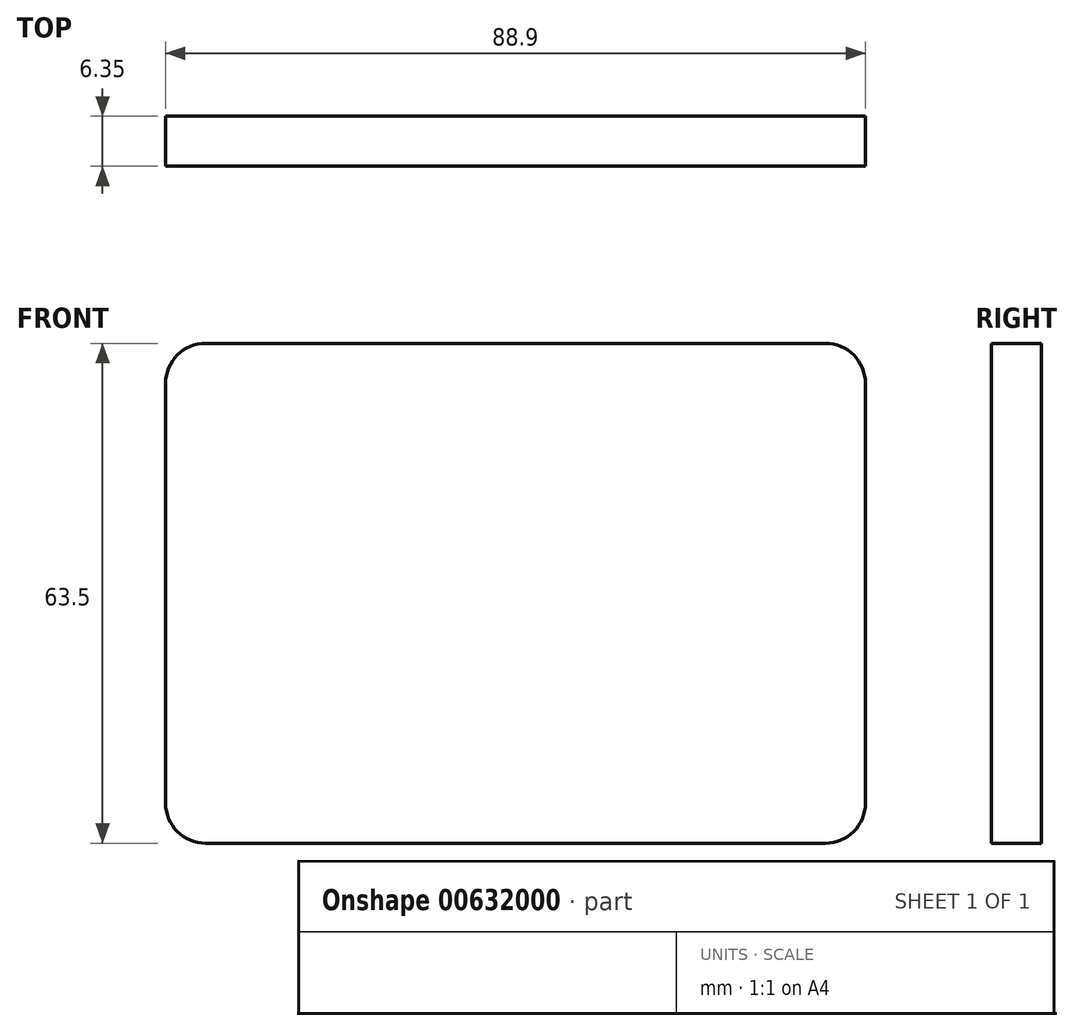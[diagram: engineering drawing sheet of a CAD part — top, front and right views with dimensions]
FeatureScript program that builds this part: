
annotation { "Feature Type Name" : "Feature", "Feature Type Description" : "" }
export const myFeature = defineFeature(function(context is Context, id is Id, definition is map)
    precondition{}
    {
        {
            var Q0;
            Q0=qCreatedBy(makeId("Front.planeOp"),FACE);
            var sketch = newSketch(context, id + "F0", { "sketchPlane" : qUnion([Q0])});
            skLineSegment(sketch, "E0.bottom", {"start": v(0, 0) * mm, "end": v(114.3, 0) * mm});
            skLineSegment(sketch, "E0.top", {"start": v(0, 88.9) * mm, "end": v(114.3, 88.9) * mm});
            skLineSegment(sketch, "E0.left", {"start": v(0, 0) * mm, "end": v(0, 88.9) * mm});
            skLineSegment(sketch, "E0.right", {"start": v(114.3, 0) * mm, "end": v(114.3, 88.9) * mm});
            skLineSegment(sketch, "E1.bottom", {"start": v(0, 0) * mm, "end": v(88.9, 0) * mm});
            skLineSegment(sketch, "E1.top", {"start": v(0, 63.5) * mm, "end": v(88.9, 63.5) * mm});
            skLineSegment(sketch, "E1.left", {"start": v(0, 0) * mm, "end": v(0, 63.5) * mm});
            skLineSegment(sketch, "E1.right", {"start": v(88.9, 0) * mm, "end": v(88.9, 63.5) * mm});
            skCircle(sketch, "E2", {"center": v(101.6, 76.2) * mm, "radius": 3.18 * mm});
            skSolve(sketch);
        }
        {
            var Q0;
            Q0=makeQuery(id+"F0.imprint","IMPRINT",FACE,{"disambiguationData":[TD([[makeQuery(id+"F0.imprint","IMPRINT",EDGE,{"derivedFrom":sQuery(id+"F0.wireOp",EDGE,"E0.bottom")}),1.0]])]});
            extrude(context, id + "F1", {"entities" : qUnion([Q0]), "depth" : 6.35 * mm, "offsetDistance" : 25.4 * mm});
        }
        {
            var Q0;
            Q0=makeQuery(id+"F1.opExtrude","SWEPT_EDGE",EDGE,{"disambiguationData":[OSD([sQuery(id+"F0.wireOp",EDGE,"E0.left"),sQuery(id+"F0.wireOp",EDGE,"E1.top"),sQuery(id+"F0.wireOp",EDGE,"E1.left")])]});
            var Q1;
            Q1=makeQuery(id+"F1.opExtrude","SWEPT_EDGE",EDGE,{"disambiguationData":[OSD([sQuery(id+"F0.wireOp",EDGE,"E0.top"),sQuery(id+"F0.wireOp",EDGE,"E0.left")])]});
            var Q2;
            Q2=makeQuery(id+"F1.opExtrude","SWEPT_EDGE",EDGE,{"disambiguationData":[OSD([sQuery(id+"F0.wireOp",EDGE,"E0.top"),sQuery(id+"F0.wireOp",EDGE,"E0.right")])]});
            var Q3;
            Q3=makeQuery(id+"F1.opExtrude","SWEPT_EDGE",EDGE,{"disambiguationData":[OSD([sQuery(id+"F0.wireOp",EDGE,"E0.bottom"),sQuery(id+"F0.wireOp",EDGE,"E0.right")])]});
            var Q4;
            Q4=makeQuery(id+"F1.opExtrude","SWEPT_EDGE",EDGE,{"disambiguationData":[OSD([sQuery(id+"F0.wireOp",EDGE,"E0.bottom"),sQuery(id+"F0.wireOp",EDGE,"E1.bottom"),sQuery(id+"F0.wireOp",EDGE,"E1.right")])]});
            var Q5;
            Q5=makeQuery(id+"F1.opExtrude","SWEPT_EDGE",EDGE,{"disambiguationData":[OSD([sQuery(id+"F0.wireOp",EDGE,"E1.top"),sQuery(id+"F0.wireOp",EDGE,"E1.right")])]});
            fillet(context, id + "F2", {"entities" : qUnion([Q0, Q1, Q2, Q3, Q4, Q5]), "radius" : 5.08 * mm, "tangentPropagation" : true, "allowEdgeOverflow" : false});
        }
        {
            var Q0;
            Q0=makeQuery(id+"F1.opExtrude","CAP_FACE",FACE,{"disambiguationData":[OSD([sQuery(id+"F0.wireOp",EDGE,"E0.bottom"),sQuery(id+"F0.wireOp",EDGE,"E0.top"),sQuery(id+"F0.wireOp",EDGE,"E0.left"),sQuery(id+"F0.wireOp",EDGE,"E0.right"),sQuery(id+"F0.wireOp",EDGE,"E1.top"),sQuery(id+"F0.wireOp",EDGE,"E1.right")])],"isStart":true});
            var sketch = newSketch(context, id + "F3", { "sketchPlane" : qUnion([Q0])});
            skCircle(sketch, "E3", {"center": v(-13.6, 76.2) * mm, "radius": 6.35 * mm});
            skPoint(sketch, "E3.centerSnap0", {"position": v(0, 76.2) * mm});
            skSolve(sketch);
        }
        {
            var Q0;
            Q0=makeQuery(id+"F3.imprint","IMPRINT",FACE,{"disambiguationData":[TD([[makeQuery(id+"F3.imprint","IMPRINT",EDGE,{"derivedFrom":sQuery(id+"F3.wireOp",EDGE,"E3")}),1.0]])]});
            var Q1;
            Q1=sQuery(id+"F3.wireOp",EDGE,"E3");
            extrude(context, id + "F4", {"entities" : qUnion([Q0]), "operationType" : NewBodyOperationType.REMOVE, "surfaceEntities" : qUnion([Q1]), "oppositeDirection" : true, "depth" : 25.4 * mm, "offsetDistance" : 25.4 * mm});
        }
    });
